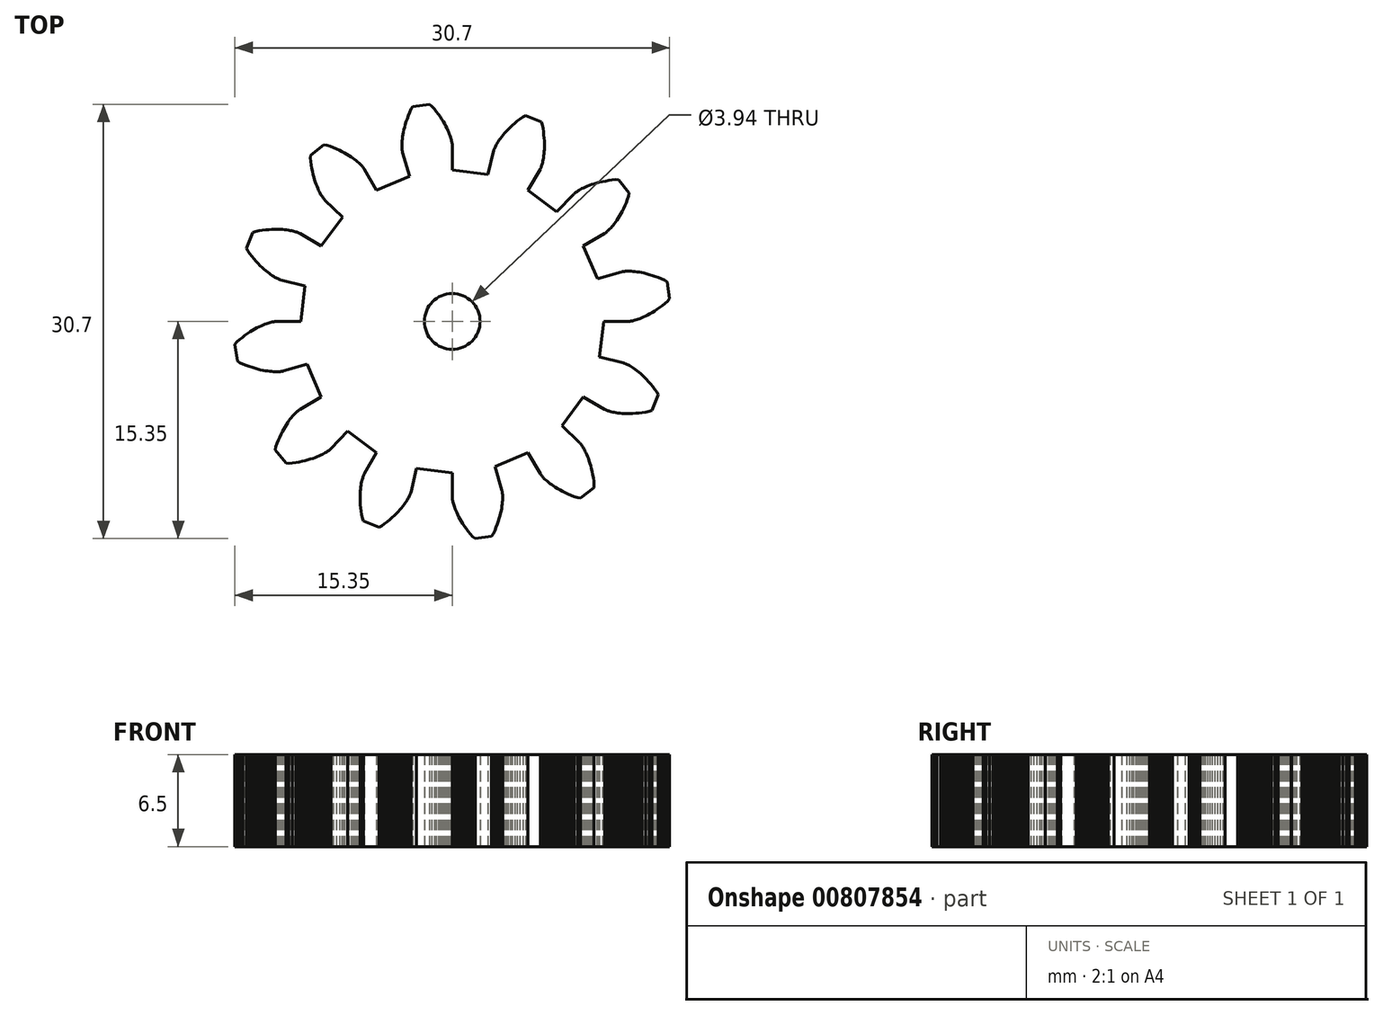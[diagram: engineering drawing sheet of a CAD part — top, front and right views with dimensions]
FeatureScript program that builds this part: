
annotation { "Feature Type Name" : "Feature", "Feature Type Description" : "" }
export const myFeature = defineFeature(function(context is Context, id is Id, definition is map)
    precondition{}
    {
        {
            var Q0;
            Q0=qCreatedBy(makeId("Top.planeOp"),FACE);
            var sketch = newSketch(context, id + "F0", { "sketchPlane" : qUnion([Q0])});
            skLineSegment(sketch, "E0", {"start": v(10.7, 0) * mm, "end": v(12.45, 0) * mm});
            skLineSegment(sketch, "E1", {"start": v(12.45, 0) * mm, "end": v(12.47, 0) * mm});
            skLineSegment(sketch, "E2", {"start": v(12.47, 0) * mm, "end": v(12.5, 0) * mm});
            skLineSegment(sketch, "E3", {"start": v(12.5, 0) * mm, "end": v(12.54, 0) * mm});
            skLineSegment(sketch, "E4", {"start": v(12.54, 0) * mm, "end": v(12.6, 0.02) * mm});
            skLineSegment(sketch, "E5", {"start": v(12.6, 0.02) * mm, "end": v(12.66, 0.03) * mm});
            skLineSegment(sketch, "E6", {"start": v(12.66, 0.03) * mm, "end": v(12.73, 0.04) * mm});
            skLineSegment(sketch, "E7", {"start": v(12.73, 0.04) * mm, "end": v(12.81, 0.06) * mm});
            skLineSegment(sketch, "E8", {"start": v(12.81, 0.06) * mm, "end": v(12.9, 0.09) * mm});
            skLineSegment(sketch, "E9", {"start": v(12.9, 0.09) * mm, "end": v(13, 0.12) * mm});
            skLineSegment(sketch, "E10", {"start": v(13, 0.12) * mm, "end": v(13.12, 0.16) * mm});
            skLineSegment(sketch, "E11", {"start": v(13.12, 0.16) * mm, "end": v(13.24, 0.2) * mm});
            skLineSegment(sketch, "E12", {"start": v(13.24, 0.2) * mm, "end": v(13.37, 0.25) * mm});
            skLineSegment(sketch, "E13", {"start": v(13.37, 0.25) * mm, "end": v(13.5, 0.31) * mm});
            skLineSegment(sketch, "E14", {"start": v(13.5, 0.31) * mm, "end": v(13.65, 0.38) * mm});
            skLineSegment(sketch, "E15", {"start": v(13.65, 0.38) * mm, "end": v(13.8, 0.46) * mm});
            skLineSegment(sketch, "E16", {"start": v(13.8, 0.46) * mm, "end": v(13.96, 0.54) * mm});
            skLineSegment(sketch, "E17", {"start": v(13.96, 0.54) * mm, "end": v(14.12, 0.64) * mm});
            skLineSegment(sketch, "E18", {"start": v(14.12, 0.64) * mm, "end": v(14.3, 0.74) * mm});
            skLineSegment(sketch, "E19", {"start": v(14.3, 0.74) * mm, "end": v(14.47, 0.86) * mm});
            skLineSegment(sketch, "E20", {"start": v(14.47, 0.86) * mm, "end": v(14.65, 0.99) * mm});
            skLineSegment(sketch, "E21", {"start": v(14.65, 0.99) * mm, "end": v(14.83, 1.13) * mm});
            skLineSegment(sketch, "E22", {"start": v(14.83, 1.13) * mm, "end": v(15.02, 1.28) * mm});
            skLineSegment(sketch, "E23", {"start": v(15.02, 1.28) * mm, "end": v(15.22, 1.44) * mm});
            skLineSegment(sketch, "E24", {"start": v(15.22, 1.44) * mm, "end": v(15.35, 1.61) * mm});
            skLineSegment(sketch, "E25", {"start": v(15.35, 1.61) * mm, "end": v(15.18, 2.78) * mm});
            skLineSegment(sketch, "E26", {"start": v(15.18, 2.78) * mm, "end": v(15, 2.9) * mm});
            skLineSegment(sketch, "E27", {"start": v(15, 2.9) * mm, "end": v(14.78, 3) * mm});
            skLineSegment(sketch, "E28", {"start": v(14.78, 3) * mm, "end": v(14.55, 3.1) * mm});
            skLineSegment(sketch, "E29", {"start": v(14.55, 3.1) * mm, "end": v(14.33, 3.18) * mm});
            skLineSegment(sketch, "E30", {"start": v(14.33, 3.18) * mm, "end": v(14.12, 3.25) * mm});
            skLineSegment(sketch, "E31", {"start": v(14.12, 3.25) * mm, "end": v(13.92, 3.32) * mm});
            skLineSegment(sketch, "E32", {"start": v(13.92, 3.32) * mm, "end": v(13.73, 3.37) * mm});
            skLineSegment(sketch, "E33", {"start": v(13.73, 3.37) * mm, "end": v(13.54, 3.41) * mm});
            skLineSegment(sketch, "E34", {"start": v(13.54, 3.41) * mm, "end": v(13.37, 3.45) * mm});
            skLineSegment(sketch, "E35", {"start": v(13.37, 3.45) * mm, "end": v(13.2, 3.48) * mm});
            skLineSegment(sketch, "E36", {"start": v(13.2, 3.48) * mm, "end": v(13.04, 3.5) * mm});
            skLineSegment(sketch, "E37", {"start": v(13.04, 3.5) * mm, "end": v(12.9, 3.53) * mm});
            skLineSegment(sketch, "E38", {"start": v(12.9, 3.53) * mm, "end": v(12.76, 3.54) * mm});
            skLineSegment(sketch, "E39", {"start": v(12.76, 3.54) * mm, "end": v(12.63, 3.55) * mm});
            skLineSegment(sketch, "E40", {"start": v(12.63, 3.55) * mm, "end": v(12.51, 3.55) * mm});
            skLineSegment(sketch, "E41", {"start": v(12.51, 3.55) * mm, "end": v(12.4, 3.55) * mm});
            skLineSegment(sketch, "E42", {"start": v(12.4, 3.55) * mm, "end": v(12.31, 3.55) * mm});
            skLineSegment(sketch, "E43", {"start": v(12.31, 3.55) * mm, "end": v(12.23, 3.55) * mm});
            skLineSegment(sketch, "E44", {"start": v(12.23, 3.55) * mm, "end": v(12.15, 3.54) * mm});
            skLineSegment(sketch, "E45", {"start": v(12.15, 3.54) * mm, "end": v(12.09, 3.53) * mm});
            skLineSegment(sketch, "E46", {"start": v(12.09, 3.53) * mm, "end": v(12.04, 3.53) * mm});
            skLineSegment(sketch, "E47", {"start": v(12.04, 3.53) * mm, "end": v(12, 3.52) * mm});
            skLineSegment(sketch, "E48", {"start": v(12, 3.52) * mm, "end": v(11.96, 3.51) * mm});
            skLineSegment(sketch, "E49", {"start": v(11.96, 3.51) * mm, "end": v(11.94, 3.5) * mm});
            skLineSegment(sketch, "E50", {"start": v(11.94, 3.5) * mm, "end": v(11.93, 3.5) * mm});
            skLineSegment(sketch, "E51", {"start": v(11.93, 3.5) * mm, "end": v(10.26, 3.02) * mm});
            skLineSegment(sketch, "E52", {"start": v(10.26, 3.02) * mm, "end": v(9.26, 5.35) * mm});
            skLineSegment(sketch, "E53", {"start": v(9.26, 5.35) * mm, "end": v(10.77, 6.22) * mm});
            skLineSegment(sketch, "E54", {"start": v(10.77, 6.22) * mm, "end": v(10.78, 6.22) * mm});
            skLineSegment(sketch, "E55", {"start": v(10.78, 6.22) * mm, "end": v(10.8, 6.24) * mm});
            skLineSegment(sketch, "E56", {"start": v(10.8, 6.24) * mm, "end": v(10.82, 6.25) * mm});
            skLineSegment(sketch, "E57", {"start": v(10.82, 6.25) * mm, "end": v(10.86, 6.28) * mm});
            skLineSegment(sketch, "E58", {"start": v(10.86, 6.28) * mm, "end": v(10.9, 6.31) * mm});
            skLineSegment(sketch, "E59", {"start": v(10.9, 6.31) * mm, "end": v(10.95, 6.35) * mm});
            skLineSegment(sketch, "E60", {"start": v(10.95, 6.35) * mm, "end": v(11, 6.4) * mm});
            skLineSegment(sketch, "E61", {"start": v(11, 6.4) * mm, "end": v(11.07, 6.46) * mm});
            skLineSegment(sketch, "E62", {"start": v(11.07, 6.46) * mm, "end": v(11.13, 6.53) * mm});
            skLineSegment(sketch, "E63", {"start": v(11.13, 6.53) * mm, "end": v(11.2, 6.6) * mm});
            skLineSegment(sketch, "E64", {"start": v(11.2, 6.6) * mm, "end": v(11.28, 6.7) * mm});
            skLineSegment(sketch, "E65", {"start": v(11.28, 6.7) * mm, "end": v(11.36, 6.8) * mm});
            skLineSegment(sketch, "E66", {"start": v(11.36, 6.8) * mm, "end": v(11.45, 6.9) * mm});
            skLineSegment(sketch, "E67", {"start": v(11.45, 6.9) * mm, "end": v(11.54, 7.02) * mm});
            skLineSegment(sketch, "E68", {"start": v(11.54, 7.02) * mm, "end": v(11.63, 7.15) * mm});
            skLineSegment(sketch, "E69", {"start": v(11.63, 7.15) * mm, "end": v(11.72, 7.3) * mm});
            skLineSegment(sketch, "E70", {"start": v(11.72, 7.3) * mm, "end": v(11.82, 7.45) * mm});
            skLineSegment(sketch, "E71", {"start": v(11.82, 7.45) * mm, "end": v(11.9, 7.61) * mm});
            skLineSegment(sketch, "E72", {"start": v(11.9, 7.61) * mm, "end": v(12, 7.79) * mm});
            skLineSegment(sketch, "E73", {"start": v(12, 7.79) * mm, "end": v(12.1, 7.98) * mm});
            skLineSegment(sketch, "E74", {"start": v(12.1, 7.98) * mm, "end": v(12.2, 8.18) * mm});
            skLineSegment(sketch, "E75", {"start": v(12.2, 8.18) * mm, "end": v(12.28, 8.4) * mm});
            skLineSegment(sketch, "E76", {"start": v(12.28, 8.4) * mm, "end": v(12.37, 8.62) * mm});
            skLineSegment(sketch, "E77", {"start": v(12.37, 8.62) * mm, "end": v(12.46, 8.86) * mm});
            skLineSegment(sketch, "E78", {"start": v(12.46, 8.86) * mm, "end": v(12.49, 9.07) * mm});
            skLineSegment(sketch, "E79", {"start": v(12.49, 9.07) * mm, "end": v(11.76, 10) * mm});
            skLineSegment(sketch, "E80", {"start": v(11.76, 10) * mm, "end": v(11.54, 10.02) * mm});
            skLineSegment(sketch, "E81", {"start": v(11.54, 10.02) * mm, "end": v(11.3, 10) * mm});
            skLineSegment(sketch, "E82", {"start": v(11.3, 10) * mm, "end": v(11.05, 9.96) * mm});
            skLineSegment(sketch, "E83", {"start": v(11.05, 9.96) * mm, "end": v(10.82, 9.92) * mm});
            skLineSegment(sketch, "E84", {"start": v(10.82, 9.92) * mm, "end": v(10.6, 9.88) * mm});
            skLineSegment(sketch, "E85", {"start": v(10.6, 9.88) * mm, "end": v(10.4, 9.83) * mm});
            skLineSegment(sketch, "E86", {"start": v(10.4, 9.83) * mm, "end": v(10.2, 9.78) * mm});
            skLineSegment(sketch, "E87", {"start": v(10.2, 9.78) * mm, "end": v(10.02, 9.73) * mm});
            skLineSegment(sketch, "E88", {"start": v(10.02, 9.73) * mm, "end": v(9.85, 9.67) * mm});
            skLineSegment(sketch, "E89", {"start": v(9.85, 9.67) * mm, "end": v(9.69, 9.62) * mm});
            skLineSegment(sketch, "E90", {"start": v(9.69, 9.62) * mm, "end": v(9.54, 9.56) * mm});
            skLineSegment(sketch, "E91", {"start": v(9.54, 9.56) * mm, "end": v(9.4, 9.5) * mm});
            skLineSegment(sketch, "E92", {"start": v(9.4, 9.5) * mm, "end": v(9.28, 9.44) * mm});
            skLineSegment(sketch, "E93", {"start": v(9.28, 9.44) * mm, "end": v(9.17, 9.39) * mm});
            skLineSegment(sketch, "E94", {"start": v(9.17, 9.39) * mm, "end": v(9.06, 9.33) * mm});
            skLineSegment(sketch, "E95", {"start": v(9.06, 9.33) * mm, "end": v(8.97, 9.28) * mm});
            skLineSegment(sketch, "E96", {"start": v(8.97, 9.28) * mm, "end": v(8.89, 9.23) * mm});
            skLineSegment(sketch, "E97", {"start": v(8.89, 9.23) * mm, "end": v(8.82, 9.18) * mm});
            skLineSegment(sketch, "E98", {"start": v(8.82, 9.18) * mm, "end": v(8.75, 9.14) * mm});
            skLineSegment(sketch, "E99", {"start": v(8.75, 9.14) * mm, "end": v(8.7, 9.1) * mm});
            skLineSegment(sketch, "E100", {"start": v(8.7, 9.1) * mm, "end": v(8.66, 9.07) * mm});
            skLineSegment(sketch, "E101", {"start": v(8.66, 9.07) * mm, "end": v(8.6, 9.02) * mm});
            skLineSegment(sketch, "E102", {"start": v(8.6, 9.02) * mm, "end": v(8.59, 9) * mm});
            skLineSegment(sketch, "E103", {"start": v(8.59, 9) * mm, "end": v(8.58, 9) * mm});
            skLineSegment(sketch, "E104", {"start": v(8.58, 9) * mm, "end": v(7.38, 7.74) * mm});
            skLineSegment(sketch, "E105", {"start": v(7.38, 7.74) * mm, "end": v(5.35, 9.26) * mm});
            skLineSegment(sketch, "E106", {"start": v(5.35, 9.26) * mm, "end": v(6.22, 10.77) * mm});
            skLineSegment(sketch, "E107", {"start": v(6.22, 10.77) * mm, "end": v(6.22, 10.78) * mm});
            skLineSegment(sketch, "E108", {"start": v(6.22, 10.78) * mm, "end": v(6.23, 10.8) * mm});
            skLineSegment(sketch, "E109", {"start": v(6.23, 10.8) * mm, "end": v(6.25, 10.83) * mm});
            skLineSegment(sketch, "E110", {"start": v(6.25, 10.83) * mm, "end": v(6.26, 10.87) * mm});
            skLineSegment(sketch, "E111", {"start": v(6.26, 10.87) * mm, "end": v(6.28, 10.92) * mm});
            skLineSegment(sketch, "E112", {"start": v(6.28, 10.92) * mm, "end": v(6.3, 10.98) * mm});
            skLineSegment(sketch, "E113", {"start": v(6.3, 10.98) * mm, "end": v(6.33, 11.05) * mm});
            skLineSegment(sketch, "E114", {"start": v(6.33, 11.05) * mm, "end": v(6.35, 11.13) * mm});
            skLineSegment(sketch, "E115", {"start": v(6.35, 11.13) * mm, "end": v(6.38, 11.22) * mm});
            skLineSegment(sketch, "E116", {"start": v(6.38, 11.22) * mm, "end": v(6.4, 11.33) * mm});
            skLineSegment(sketch, "E117", {"start": v(6.4, 11.33) * mm, "end": v(6.42, 11.44) * mm});
            skLineSegment(sketch, "E118", {"start": v(6.42, 11.44) * mm, "end": v(6.45, 11.57) * mm});
            skLineSegment(sketch, "E119", {"start": v(6.45, 11.57) * mm, "end": v(6.46, 11.7) * mm});
            skLineSegment(sketch, "E120", {"start": v(6.46, 11.7) * mm, "end": v(6.48, 11.85) * mm});
            skLineSegment(sketch, "E121", {"start": v(6.48, 11.85) * mm, "end": v(6.5, 12) * mm});
            skLineSegment(sketch, "E122", {"start": v(6.5, 12) * mm, "end": v(6.5, 12.18) * mm});
            skLineSegment(sketch, "E123", {"start": v(6.5, 12.18) * mm, "end": v(6.5, 12.36) * mm});
            skLineSegment(sketch, "E124", {"start": v(6.5, 12.36) * mm, "end": v(6.5, 12.55) * mm});
            skLineSegment(sketch, "E125", {"start": v(6.5, 12.55) * mm, "end": v(6.5, 12.75) * mm});
            skLineSegment(sketch, "E126", {"start": v(6.5, 12.75) * mm, "end": v(6.49, 12.96) * mm});
            skLineSegment(sketch, "E127", {"start": v(6.49, 12.96) * mm, "end": v(6.47, 13.18) * mm});
            skLineSegment(sketch, "E128", {"start": v(6.47, 13.18) * mm, "end": v(6.44, 13.41) * mm});
            skLineSegment(sketch, "E129", {"start": v(6.44, 13.41) * mm, "end": v(6.4, 13.65) * mm});
            skLineSegment(sketch, "E130", {"start": v(6.4, 13.65) * mm, "end": v(6.36, 13.9) * mm});
            skLineSegment(sketch, "E131", {"start": v(6.36, 13.9) * mm, "end": v(6.28, 14.1) * mm});
            skLineSegment(sketch, "E132", {"start": v(6.28, 14.1) * mm, "end": v(5.18, 14.54) * mm});
            skLineSegment(sketch, "E133", {"start": v(5.18, 14.54) * mm, "end": v(4.99, 14.45) * mm});
            skLineSegment(sketch, "E134", {"start": v(4.99, 14.45) * mm, "end": v(4.78, 14.3) * mm});
            skLineSegment(sketch, "E135", {"start": v(4.78, 14.3) * mm, "end": v(4.6, 14.15) * mm});
            skLineSegment(sketch, "E136", {"start": v(4.6, 14.15) * mm, "end": v(4.41, 14) * mm});
            skLineSegment(sketch, "E137", {"start": v(4.41, 14) * mm, "end": v(4.24, 13.86) * mm});
            skLineSegment(sketch, "E138", {"start": v(4.24, 13.86) * mm, "end": v(4.09, 13.71) * mm});
            skLineSegment(sketch, "E139", {"start": v(4.09, 13.71) * mm, "end": v(3.95, 13.57) * mm});
            skLineSegment(sketch, "E140", {"start": v(3.95, 13.57) * mm, "end": v(3.81, 13.43) * mm});
            skLineSegment(sketch, "E141", {"start": v(3.81, 13.43) * mm, "end": v(3.7, 13.3) * mm});
            skLineSegment(sketch, "E142", {"start": v(3.7, 13.3) * mm, "end": v(3.58, 13.17) * mm});
            skLineSegment(sketch, "E143", {"start": v(3.58, 13.17) * mm, "end": v(3.48, 13.05) * mm});
            skLineSegment(sketch, "E144", {"start": v(3.48, 13.05) * mm, "end": v(3.4, 12.93) * mm});
            skLineSegment(sketch, "E145", {"start": v(3.4, 12.93) * mm, "end": v(3.31, 12.82) * mm});
            skLineSegment(sketch, "E146", {"start": v(3.31, 12.82) * mm, "end": v(3.24, 12.71) * mm});
            skLineSegment(sketch, "E147", {"start": v(3.24, 12.71) * mm, "end": v(3.18, 12.61) * mm});
            skLineSegment(sketch, "E148", {"start": v(3.18, 12.61) * mm, "end": v(3.13, 12.52) * mm});
            skLineSegment(sketch, "E149", {"start": v(3.13, 12.52) * mm, "end": v(3.08, 12.44) * mm});
            skLineSegment(sketch, "E150", {"start": v(3.08, 12.44) * mm, "end": v(3.04, 12.36) * mm});
            skLineSegment(sketch, "E151", {"start": v(3.04, 12.36) * mm, "end": v(3, 12.3) * mm});
            skLineSegment(sketch, "E152", {"start": v(3, 12.3) * mm, "end": v(2.98, 12.24) * mm});
            skLineSegment(sketch, "E153", {"start": v(2.98, 12.24) * mm, "end": v(2.96, 12.19) * mm});
            skLineSegment(sketch, "E154", {"start": v(2.96, 12.19) * mm, "end": v(2.95, 12.15) * mm});
            skLineSegment(sketch, "E155", {"start": v(2.95, 12.15) * mm, "end": v(2.94, 12.12) * mm});
            skLineSegment(sketch, "E156", {"start": v(2.94, 12.12) * mm, "end": v(2.93, 12.1) * mm});
            skLineSegment(sketch, "E157", {"start": v(2.93, 12.1) * mm, "end": v(2.93, 12.08) * mm});
            skLineSegment(sketch, "E158", {"start": v(2.93, 12.08) * mm, "end": v(2.52, 10.4) * mm});
            skLineSegment(sketch, "E159", {"start": v(2.52, 10.4) * mm, "end": v(0, 10.7) * mm});
            skLineSegment(sketch, "E160", {"start": v(0, 10.7) * mm, "end": v(0, 12.45) * mm});
            skLineSegment(sketch, "E161", {"start": v(0, 12.45) * mm, "end": v(0, 12.47) * mm});
            skLineSegment(sketch, "E162", {"start": v(0, 12.47) * mm, "end": v(0, 12.5) * mm});
            skLineSegment(sketch, "E163", {"start": v(0, 12.5) * mm, "end": v(0, 12.54) * mm});
            skLineSegment(sketch, "E164", {"start": v(0, 12.54) * mm, "end": v(-0.02, 12.6) * mm});
            skLineSegment(sketch, "E165", {"start": v(-0.02, 12.6) * mm, "end": v(-0.03, 12.66) * mm});
            skLineSegment(sketch, "E166", {"start": v(-0.03, 12.66) * mm, "end": v(-0.04, 12.73) * mm});
            skLineSegment(sketch, "E167", {"start": v(-0.04, 12.73) * mm, "end": v(-0.06, 12.81) * mm});
            skLineSegment(sketch, "E168", {"start": v(-0.06, 12.81) * mm, "end": v(-0.09, 12.9) * mm});
            skLineSegment(sketch, "E169", {"start": v(-0.09, 12.9) * mm, "end": v(-0.12, 13) * mm});
            skLineSegment(sketch, "E170", {"start": v(-0.12, 13) * mm, "end": v(-0.16, 13.12) * mm});
            skLineSegment(sketch, "E171", {"start": v(-0.16, 13.12) * mm, "end": v(-0.2, 13.24) * mm});
            skLineSegment(sketch, "E172", {"start": v(-0.2, 13.24) * mm, "end": v(-0.25, 13.37) * mm});
            skLineSegment(sketch, "E173", {"start": v(-0.25, 13.37) * mm, "end": v(-0.31, 13.5) * mm});
            skLineSegment(sketch, "E174", {"start": v(-0.31, 13.5) * mm, "end": v(-0.38, 13.65) * mm});
            skLineSegment(sketch, "E175", {"start": v(-0.38, 13.65) * mm, "end": v(-0.46, 13.8) * mm});
            skLineSegment(sketch, "E176", {"start": v(-0.46, 13.8) * mm, "end": v(-0.54, 13.96) * mm});
            skLineSegment(sketch, "E177", {"start": v(-0.54, 13.96) * mm, "end": v(-0.64, 14.12) * mm});
            skLineSegment(sketch, "E178", {"start": v(-0.64, 14.12) * mm, "end": v(-0.74, 14.3) * mm});
            skLineSegment(sketch, "E179", {"start": v(-0.74, 14.3) * mm, "end": v(-0.86, 14.47) * mm});
            skLineSegment(sketch, "E180", {"start": v(-0.86, 14.47) * mm, "end": v(-0.99, 14.65) * mm});
            skLineSegment(sketch, "E181", {"start": v(-0.99, 14.65) * mm, "end": v(-1.13, 14.83) * mm});
            skLineSegment(sketch, "E182", {"start": v(-1.13, 14.83) * mm, "end": v(-1.28, 15.02) * mm});
            skLineSegment(sketch, "E183", {"start": v(-1.28, 15.02) * mm, "end": v(-1.44, 15.22) * mm});
            skLineSegment(sketch, "E184", {"start": v(-1.44, 15.22) * mm, "end": v(-1.61, 15.35) * mm});
            skLineSegment(sketch, "E185", {"start": v(-1.61, 15.35) * mm, "end": v(-2.78, 15.18) * mm});
            skLineSegment(sketch, "E186", {"start": v(-2.78, 15.18) * mm, "end": v(-2.9, 15) * mm});
            skLineSegment(sketch, "E187", {"start": v(-2.9, 15) * mm, "end": v(-3, 14.78) * mm});
            skLineSegment(sketch, "E188", {"start": v(-3, 14.78) * mm, "end": v(-3.1, 14.55) * mm});
            skLineSegment(sketch, "E189", {"start": v(-3.1, 14.55) * mm, "end": v(-3.18, 14.33) * mm});
            skLineSegment(sketch, "E190", {"start": v(-3.18, 14.33) * mm, "end": v(-3.25, 14.12) * mm});
            skLineSegment(sketch, "E191", {"start": v(-3.25, 14.12) * mm, "end": v(-3.32, 13.92) * mm});
            skLineSegment(sketch, "E192", {"start": v(-3.32, 13.92) * mm, "end": v(-3.37, 13.73) * mm});
            skLineSegment(sketch, "E193", {"start": v(-3.37, 13.73) * mm, "end": v(-3.41, 13.54) * mm});
            skLineSegment(sketch, "E194", {"start": v(-3.41, 13.54) * mm, "end": v(-3.45, 13.37) * mm});
            skLineSegment(sketch, "E195", {"start": v(-3.45, 13.37) * mm, "end": v(-3.48, 13.2) * mm});
            skLineSegment(sketch, "E196", {"start": v(-3.48, 13.2) * mm, "end": v(-3.5, 13.04) * mm});
            skLineSegment(sketch, "E197", {"start": v(-3.5, 13.04) * mm, "end": v(-3.53, 12.9) * mm});
            skLineSegment(sketch, "E198", {"start": v(-3.53, 12.9) * mm, "end": v(-3.54, 12.76) * mm});
            skLineSegment(sketch, "E199", {"start": v(-3.54, 12.76) * mm, "end": v(-3.55, 12.63) * mm});
            skLineSegment(sketch, "E200", {"start": v(-3.55, 12.63) * mm, "end": v(-3.55, 12.51) * mm});
            skLineSegment(sketch, "E201", {"start": v(-3.55, 12.51) * mm, "end": v(-3.55, 12.4) * mm});
            skLineSegment(sketch, "E202", {"start": v(-3.55, 12.4) * mm, "end": v(-3.55, 12.31) * mm});
            skLineSegment(sketch, "E203", {"start": v(-3.55, 12.31) * mm, "end": v(-3.55, 12.23) * mm});
            skLineSegment(sketch, "E204", {"start": v(-3.55, 12.23) * mm, "end": v(-3.54, 12.15) * mm});
            skLineSegment(sketch, "E205", {"start": v(-3.54, 12.15) * mm, "end": v(-3.53, 12.09) * mm});
            skLineSegment(sketch, "E206", {"start": v(-3.53, 12.09) * mm, "end": v(-3.53, 12.04) * mm});
            skLineSegment(sketch, "E207", {"start": v(-3.53, 12.04) * mm, "end": v(-3.52, 12) * mm});
            skLineSegment(sketch, "E208", {"start": v(-3.52, 12) * mm, "end": v(-3.51, 11.96) * mm});
            skLineSegment(sketch, "E209", {"start": v(-3.51, 11.96) * mm, "end": v(-3.5, 11.94) * mm});
            skLineSegment(sketch, "E210", {"start": v(-3.5, 11.94) * mm, "end": v(-3.5, 11.93) * mm});
            skLineSegment(sketch, "E211", {"start": v(-3.5, 11.93) * mm, "end": v(-3.02, 10.26) * mm});
            skLineSegment(sketch, "E212", {"start": v(-3.02, 10.26) * mm, "end": v(-5.35, 9.26) * mm});
            skLineSegment(sketch, "E213", {"start": v(-5.35, 9.26) * mm, "end": v(-6.22, 10.77) * mm});
            skLineSegment(sketch, "E214", {"start": v(-6.22, 10.77) * mm, "end": v(-6.22, 10.78) * mm});
            skLineSegment(sketch, "E215", {"start": v(-6.22, 10.78) * mm, "end": v(-6.24, 10.8) * mm});
            skLineSegment(sketch, "E216", {"start": v(-6.24, 10.8) * mm, "end": v(-6.25, 10.82) * mm});
            skLineSegment(sketch, "E217", {"start": v(-6.25, 10.82) * mm, "end": v(-6.28, 10.86) * mm});
            skLineSegment(sketch, "E218", {"start": v(-6.28, 10.86) * mm, "end": v(-6.31, 10.9) * mm});
            skLineSegment(sketch, "E219", {"start": v(-6.31, 10.9) * mm, "end": v(-6.35, 10.95) * mm});
            skLineSegment(sketch, "E220", {"start": v(-6.35, 10.95) * mm, "end": v(-6.4, 11) * mm});
            skLineSegment(sketch, "E221", {"start": v(-6.4, 11) * mm, "end": v(-6.46, 11.07) * mm});
            skLineSegment(sketch, "E222", {"start": v(-6.46, 11.07) * mm, "end": v(-6.53, 11.13) * mm});
            skLineSegment(sketch, "E223", {"start": v(-6.53, 11.13) * mm, "end": v(-6.6, 11.2) * mm});
            skLineSegment(sketch, "E224", {"start": v(-6.6, 11.2) * mm, "end": v(-6.7, 11.28) * mm});
            skLineSegment(sketch, "E225", {"start": v(-6.7, 11.28) * mm, "end": v(-6.8, 11.36) * mm});
            skLineSegment(sketch, "E226", {"start": v(-6.8, 11.36) * mm, "end": v(-6.9, 11.45) * mm});
            skLineSegment(sketch, "E227", {"start": v(-6.9, 11.45) * mm, "end": v(-7.02, 11.54) * mm});
            skLineSegment(sketch, "E228", {"start": v(-7.02, 11.54) * mm, "end": v(-7.15, 11.63) * mm});
            skLineSegment(sketch, "E229", {"start": v(-7.15, 11.63) * mm, "end": v(-7.3, 11.72) * mm});
            skLineSegment(sketch, "E230", {"start": v(-7.3, 11.72) * mm, "end": v(-7.45, 11.82) * mm});
            skLineSegment(sketch, "E231", {"start": v(-7.45, 11.82) * mm, "end": v(-7.61, 11.9) * mm});
            skLineSegment(sketch, "E232", {"start": v(-7.61, 11.9) * mm, "end": v(-7.79, 12) * mm});
            skLineSegment(sketch, "E233", {"start": v(-7.79, 12) * mm, "end": v(-7.98, 12.1) * mm});
            skLineSegment(sketch, "E234", {"start": v(-7.98, 12.1) * mm, "end": v(-8.18, 12.2) * mm});
            skLineSegment(sketch, "E235", {"start": v(-8.18, 12.2) * mm, "end": v(-8.4, 12.28) * mm});
            skLineSegment(sketch, "E236", {"start": v(-8.4, 12.28) * mm, "end": v(-8.62, 12.37) * mm});
            skLineSegment(sketch, "E237", {"start": v(-8.62, 12.37) * mm, "end": v(-8.86, 12.46) * mm});
            skLineSegment(sketch, "E238", {"start": v(-8.86, 12.46) * mm, "end": v(-9.07, 12.49) * mm});
            skLineSegment(sketch, "E239", {"start": v(-9.07, 12.49) * mm, "end": v(-10, 11.76) * mm});
            skLineSegment(sketch, "E240", {"start": v(-10, 11.76) * mm, "end": v(-10.02, 11.54) * mm});
            skLineSegment(sketch, "E241", {"start": v(-10.02, 11.54) * mm, "end": v(-10, 11.3) * mm});
            skLineSegment(sketch, "E242", {"start": v(-10, 11.3) * mm, "end": v(-9.96, 11.05) * mm});
            skLineSegment(sketch, "E243", {"start": v(-9.96, 11.05) * mm, "end": v(-9.92, 10.82) * mm});
            skLineSegment(sketch, "E244", {"start": v(-9.92, 10.82) * mm, "end": v(-9.88, 10.6) * mm});
            skLineSegment(sketch, "E245", {"start": v(-9.88, 10.6) * mm, "end": v(-9.83, 10.4) * mm});
            skLineSegment(sketch, "E246", {"start": v(-9.83, 10.4) * mm, "end": v(-9.78, 10.2) * mm});
            skLineSegment(sketch, "E247", {"start": v(-9.78, 10.2) * mm, "end": v(-9.73, 10.02) * mm});
            skLineSegment(sketch, "E248", {"start": v(-9.73, 10.02) * mm, "end": v(-9.67, 9.85) * mm});
            skLineSegment(sketch, "E249", {"start": v(-9.67, 9.85) * mm, "end": v(-9.62, 9.69) * mm});
            skLineSegment(sketch, "E250", {"start": v(-9.62, 9.69) * mm, "end": v(-9.56, 9.54) * mm});
            skLineSegment(sketch, "E251", {"start": v(-9.56, 9.54) * mm, "end": v(-9.5, 9.4) * mm});
            skLineSegment(sketch, "E252", {"start": v(-9.5, 9.4) * mm, "end": v(-9.44, 9.28) * mm});
            skLineSegment(sketch, "E253", {"start": v(-9.44, 9.28) * mm, "end": v(-9.39, 9.17) * mm});
            skLineSegment(sketch, "E254", {"start": v(-9.39, 9.17) * mm, "end": v(-9.33, 9.06) * mm});
            skLineSegment(sketch, "E255", {"start": v(-9.33, 9.06) * mm, "end": v(-9.28, 8.97) * mm});
            skLineSegment(sketch, "E256", {"start": v(-9.28, 8.97) * mm, "end": v(-9.23, 8.89) * mm});
            skLineSegment(sketch, "E257", {"start": v(-9.23, 8.89) * mm, "end": v(-9.18, 8.82) * mm});
            skLineSegment(sketch, "E258", {"start": v(-9.18, 8.82) * mm, "end": v(-9.14, 8.75) * mm});
            skLineSegment(sketch, "E259", {"start": v(-9.14, 8.75) * mm, "end": v(-9.1, 8.7) * mm});
            skLineSegment(sketch, "E260", {"start": v(-9.1, 8.7) * mm, "end": v(-9.07, 8.66) * mm});
            skLineSegment(sketch, "E261", {"start": v(-9.07, 8.66) * mm, "end": v(-9.02, 8.6) * mm});
            skLineSegment(sketch, "E262", {"start": v(-9.02, 8.6) * mm, "end": v(-9, 8.59) * mm});
            skLineSegment(sketch, "E263", {"start": v(-9, 8.59) * mm, "end": v(-9, 8.58) * mm});
            skLineSegment(sketch, "E264", {"start": v(-9, 8.58) * mm, "end": v(-7.74, 7.38) * mm});
            skLineSegment(sketch, "E265", {"start": v(-7.74, 7.38) * mm, "end": v(-9.26, 5.35) * mm});
            skLineSegment(sketch, "E266", {"start": v(-9.26, 5.35) * mm, "end": v(-10.77, 6.22) * mm});
            skLineSegment(sketch, "E267", {"start": v(-10.77, 6.22) * mm, "end": v(-10.78, 6.22) * mm});
            skLineSegment(sketch, "E268", {"start": v(-10.78, 6.22) * mm, "end": v(-10.8, 6.23) * mm});
            skLineSegment(sketch, "E269", {"start": v(-10.8, 6.23) * mm, "end": v(-10.83, 6.25) * mm});
            skLineSegment(sketch, "E270", {"start": v(-10.83, 6.25) * mm, "end": v(-10.87, 6.26) * mm});
            skLineSegment(sketch, "E271", {"start": v(-10.87, 6.26) * mm, "end": v(-10.92, 6.28) * mm});
            skLineSegment(sketch, "E272", {"start": v(-10.92, 6.28) * mm, "end": v(-10.98, 6.3) * mm});
            skLineSegment(sketch, "E273", {"start": v(-10.98, 6.3) * mm, "end": v(-11.05, 6.33) * mm});
            skLineSegment(sketch, "E274", {"start": v(-11.05, 6.33) * mm, "end": v(-11.13, 6.35) * mm});
            skLineSegment(sketch, "E275", {"start": v(-11.13, 6.35) * mm, "end": v(-11.22, 6.38) * mm});
            skLineSegment(sketch, "E276", {"start": v(-11.22, 6.38) * mm, "end": v(-11.33, 6.4) * mm});
            skLineSegment(sketch, "E277", {"start": v(-11.33, 6.4) * mm, "end": v(-11.44, 6.42) * mm});
            skLineSegment(sketch, "E278", {"start": v(-11.44, 6.42) * mm, "end": v(-11.57, 6.45) * mm});
            skLineSegment(sketch, "E279", {"start": v(-11.57, 6.45) * mm, "end": v(-11.7, 6.46) * mm});
            skLineSegment(sketch, "E280", {"start": v(-11.7, 6.46) * mm, "end": v(-11.85, 6.48) * mm});
            skLineSegment(sketch, "E281", {"start": v(-11.85, 6.48) * mm, "end": v(-12, 6.5) * mm});
            skLineSegment(sketch, "E282", {"start": v(-12, 6.5) * mm, "end": v(-12.18, 6.5) * mm});
            skLineSegment(sketch, "E283", {"start": v(-12.18, 6.5) * mm, "end": v(-12.36, 6.5) * mm});
            skLineSegment(sketch, "E284", {"start": v(-12.36, 6.5) * mm, "end": v(-12.55, 6.5) * mm});
            skLineSegment(sketch, "E285", {"start": v(-12.55, 6.5) * mm, "end": v(-12.75, 6.5) * mm});
            skLineSegment(sketch, "E286", {"start": v(-12.75, 6.5) * mm, "end": v(-12.96, 6.49) * mm});
            skLineSegment(sketch, "E287", {"start": v(-12.96, 6.49) * mm, "end": v(-13.18, 6.47) * mm});
            skLineSegment(sketch, "E288", {"start": v(-13.18, 6.47) * mm, "end": v(-13.41, 6.44) * mm});
            skLineSegment(sketch, "E289", {"start": v(-13.41, 6.44) * mm, "end": v(-13.65, 6.4) * mm});
            skLineSegment(sketch, "E290", {"start": v(-13.65, 6.4) * mm, "end": v(-13.9, 6.36) * mm});
            skLineSegment(sketch, "E291", {"start": v(-13.9, 6.36) * mm, "end": v(-14.1, 6.28) * mm});
            skLineSegment(sketch, "E292", {"start": v(-14.1, 6.28) * mm, "end": v(-14.54, 5.18) * mm});
            skLineSegment(sketch, "E293", {"start": v(-14.54, 5.18) * mm, "end": v(-14.45, 4.99) * mm});
            skLineSegment(sketch, "E294", {"start": v(-14.45, 4.99) * mm, "end": v(-14.3, 4.78) * mm});
            skLineSegment(sketch, "E295", {"start": v(-14.3, 4.78) * mm, "end": v(-14.15, 4.6) * mm});
            skLineSegment(sketch, "E296", {"start": v(-14.15, 4.6) * mm, "end": v(-14, 4.41) * mm});
            skLineSegment(sketch, "E297", {"start": v(-14, 4.41) * mm, "end": v(-13.86, 4.24) * mm});
            skLineSegment(sketch, "E298", {"start": v(-13.86, 4.24) * mm, "end": v(-13.71, 4.09) * mm});
            skLineSegment(sketch, "E299", {"start": v(-13.71, 4.09) * mm, "end": v(-13.57, 3.95) * mm});
            skLineSegment(sketch, "E300", {"start": v(-13.57, 3.95) * mm, "end": v(-13.43, 3.81) * mm});
            skLineSegment(sketch, "E301", {"start": v(-13.43, 3.81) * mm, "end": v(-13.3, 3.7) * mm});
            skLineSegment(sketch, "E302", {"start": v(-13.3, 3.7) * mm, "end": v(-13.17, 3.58) * mm});
            skLineSegment(sketch, "E303", {"start": v(-13.17, 3.58) * mm, "end": v(-13.05, 3.48) * mm});
            skLineSegment(sketch, "E304", {"start": v(-13.05, 3.48) * mm, "end": v(-12.93, 3.4) * mm});
            skLineSegment(sketch, "E305", {"start": v(-12.93, 3.4) * mm, "end": v(-12.82, 3.31) * mm});
            skLineSegment(sketch, "E306", {"start": v(-12.82, 3.31) * mm, "end": v(-12.71, 3.24) * mm});
            skLineSegment(sketch, "E307", {"start": v(-12.71, 3.24) * mm, "end": v(-12.61, 3.18) * mm});
            skLineSegment(sketch, "E308", {"start": v(-12.61, 3.18) * mm, "end": v(-12.52, 3.13) * mm});
            skLineSegment(sketch, "E309", {"start": v(-12.52, 3.13) * mm, "end": v(-12.44, 3.08) * mm});
            skLineSegment(sketch, "E310", {"start": v(-12.44, 3.08) * mm, "end": v(-12.36, 3.04) * mm});
            skLineSegment(sketch, "E311", {"start": v(-12.36, 3.04) * mm, "end": v(-12.3, 3) * mm});
            skLineSegment(sketch, "E312", {"start": v(-12.3, 3) * mm, "end": v(-12.24, 2.98) * mm});
            skLineSegment(sketch, "E313", {"start": v(-12.24, 2.98) * mm, "end": v(-12.19, 2.96) * mm});
            skLineSegment(sketch, "E314", {"start": v(-12.19, 2.96) * mm, "end": v(-12.15, 2.95) * mm});
            skLineSegment(sketch, "E315", {"start": v(-12.15, 2.95) * mm, "end": v(-12.12, 2.94) * mm});
            skLineSegment(sketch, "E316", {"start": v(-12.12, 2.94) * mm, "end": v(-12.1, 2.93) * mm});
            skLineSegment(sketch, "E317", {"start": v(-12.1, 2.93) * mm, "end": v(-12.08, 2.93) * mm});
            skLineSegment(sketch, "E318", {"start": v(-12.08, 2.93) * mm, "end": v(-10.4, 2.52) * mm});
            skLineSegment(sketch, "E319", {"start": v(-10.4, 2.52) * mm, "end": v(-10.7, 0) * mm});
            skLineSegment(sketch, "E320", {"start": v(-10.7, 0) * mm, "end": v(-12.45, 0) * mm});
            skLineSegment(sketch, "E321", {"start": v(-12.45, 0) * mm, "end": v(-12.47, 0) * mm});
            skLineSegment(sketch, "E322", {"start": v(-12.47, 0) * mm, "end": v(-12.5, 0) * mm});
            skLineSegment(sketch, "E323", {"start": v(-12.5, 0) * mm, "end": v(-12.54, 0) * mm});
            skLineSegment(sketch, "E324", {"start": v(-12.54, 0) * mm, "end": v(-12.6, -0.02) * mm});
            skLineSegment(sketch, "E325", {"start": v(-12.6, -0.02) * mm, "end": v(-12.66, -0.03) * mm});
            skLineSegment(sketch, "E326", {"start": v(-12.66, -0.03) * mm, "end": v(-12.73, -0.04) * mm});
            skLineSegment(sketch, "E327", {"start": v(-12.73, -0.04) * mm, "end": v(-12.81, -0.06) * mm});
            skLineSegment(sketch, "E328", {"start": v(-12.81, -0.06) * mm, "end": v(-12.9, -0.09) * mm});
            skLineSegment(sketch, "E329", {"start": v(-12.9, -0.09) * mm, "end": v(-13, -0.12) * mm});
            skLineSegment(sketch, "E330", {"start": v(-13, -0.12) * mm, "end": v(-13.12, -0.16) * mm});
            skLineSegment(sketch, "E331", {"start": v(-13.12, -0.16) * mm, "end": v(-13.24, -0.2) * mm});
            skLineSegment(sketch, "E332", {"start": v(-13.24, -0.2) * mm, "end": v(-13.37, -0.25) * mm});
            skLineSegment(sketch, "E333", {"start": v(-13.37, -0.25) * mm, "end": v(-13.5, -0.31) * mm});
            skLineSegment(sketch, "E334", {"start": v(-13.5, -0.31) * mm, "end": v(-13.65, -0.38) * mm});
            skLineSegment(sketch, "E335", {"start": v(-13.65, -0.38) * mm, "end": v(-13.8, -0.46) * mm});
            skLineSegment(sketch, "E336", {"start": v(-13.8, -0.46) * mm, "end": v(-13.96, -0.54) * mm});
            skLineSegment(sketch, "E337", {"start": v(-13.96, -0.54) * mm, "end": v(-14.12, -0.64) * mm});
            skLineSegment(sketch, "E338", {"start": v(-14.12, -0.64) * mm, "end": v(-14.3, -0.74) * mm});
            skLineSegment(sketch, "E339", {"start": v(-14.3, -0.74) * mm, "end": v(-14.47, -0.86) * mm});
            skLineSegment(sketch, "E340", {"start": v(-14.47, -0.86) * mm, "end": v(-14.65, -0.99) * mm});
            skLineSegment(sketch, "E341", {"start": v(-14.65, -0.99) * mm, "end": v(-14.83, -1.13) * mm});
            skLineSegment(sketch, "E342", {"start": v(-14.83, -1.13) * mm, "end": v(-15.02, -1.28) * mm});
            skLineSegment(sketch, "E343", {"start": v(-15.02, -1.28) * mm, "end": v(-15.22, -1.44) * mm});
            skLineSegment(sketch, "E344", {"start": v(-15.22, -1.44) * mm, "end": v(-15.35, -1.61) * mm});
            skLineSegment(sketch, "E345", {"start": v(-15.35, -1.61) * mm, "end": v(-15.18, -2.78) * mm});
            skLineSegment(sketch, "E346", {"start": v(-15.18, -2.78) * mm, "end": v(-15, -2.9) * mm});
            skLineSegment(sketch, "E347", {"start": v(-15, -2.9) * mm, "end": v(-14.78, -3) * mm});
            skLineSegment(sketch, "E348", {"start": v(-14.78, -3) * mm, "end": v(-14.55, -3.1) * mm});
            skLineSegment(sketch, "E349", {"start": v(-14.55, -3.1) * mm, "end": v(-14.33, -3.18) * mm});
            skLineSegment(sketch, "E350", {"start": v(-14.33, -3.18) * mm, "end": v(-14.12, -3.25) * mm});
            skLineSegment(sketch, "E351", {"start": v(-14.12, -3.25) * mm, "end": v(-13.92, -3.32) * mm});
            skLineSegment(sketch, "E352", {"start": v(-13.92, -3.32) * mm, "end": v(-13.73, -3.37) * mm});
            skLineSegment(sketch, "E353", {"start": v(-13.73, -3.37) * mm, "end": v(-13.54, -3.41) * mm});
            skLineSegment(sketch, "E354", {"start": v(-13.54, -3.41) * mm, "end": v(-13.37, -3.45) * mm});
            skLineSegment(sketch, "E355", {"start": v(-13.37, -3.45) * mm, "end": v(-13.2, -3.48) * mm});
            skLineSegment(sketch, "E356", {"start": v(-13.2, -3.48) * mm, "end": v(-13.04, -3.5) * mm});
            skLineSegment(sketch, "E357", {"start": v(-13.04, -3.5) * mm, "end": v(-12.9, -3.53) * mm});
            skLineSegment(sketch, "E358", {"start": v(-12.9, -3.53) * mm, "end": v(-12.76, -3.54) * mm});
            skLineSegment(sketch, "E359", {"start": v(-12.76, -3.54) * mm, "end": v(-12.63, -3.55) * mm});
            skLineSegment(sketch, "E360", {"start": v(-12.63, -3.55) * mm, "end": v(-12.51, -3.55) * mm});
            skLineSegment(sketch, "E361", {"start": v(-12.51, -3.55) * mm, "end": v(-12.4, -3.55) * mm});
            skLineSegment(sketch, "E362", {"start": v(-12.4, -3.55) * mm, "end": v(-12.31, -3.55) * mm});
            skLineSegment(sketch, "E363", {"start": v(-12.31, -3.55) * mm, "end": v(-12.23, -3.55) * mm});
            skLineSegment(sketch, "E364", {"start": v(-12.23, -3.55) * mm, "end": v(-12.15, -3.54) * mm});
            skLineSegment(sketch, "E365", {"start": v(-12.15, -3.54) * mm, "end": v(-12.09, -3.53) * mm});
            skLineSegment(sketch, "E366", {"start": v(-12.09, -3.53) * mm, "end": v(-12.04, -3.53) * mm});
            skLineSegment(sketch, "E367", {"start": v(-12.04, -3.53) * mm, "end": v(-12, -3.52) * mm});
            skLineSegment(sketch, "E368", {"start": v(-12, -3.52) * mm, "end": v(-11.96, -3.51) * mm});
            skLineSegment(sketch, "E369", {"start": v(-11.96, -3.51) * mm, "end": v(-11.94, -3.5) * mm});
            skLineSegment(sketch, "E370", {"start": v(-11.94, -3.5) * mm, "end": v(-11.93, -3.5) * mm});
            skLineSegment(sketch, "E371", {"start": v(-11.93, -3.5) * mm, "end": v(-10.26, -3.02) * mm});
            skLineSegment(sketch, "E372", {"start": v(-10.26, -3.02) * mm, "end": v(-9.26, -5.35) * mm});
            skLineSegment(sketch, "E373", {"start": v(-9.26, -5.35) * mm, "end": v(-10.77, -6.22) * mm});
            skLineSegment(sketch, "E374", {"start": v(-10.77, -6.22) * mm, "end": v(-10.78, -6.22) * mm});
            skLineSegment(sketch, "E375", {"start": v(-10.78, -6.22) * mm, "end": v(-10.8, -6.24) * mm});
            skLineSegment(sketch, "E376", {"start": v(-10.8, -6.24) * mm, "end": v(-10.82, -6.25) * mm});
            skLineSegment(sketch, "E377", {"start": v(-10.82, -6.25) * mm, "end": v(-10.86, -6.28) * mm});
            skLineSegment(sketch, "E378", {"start": v(-10.86, -6.28) * mm, "end": v(-10.9, -6.31) * mm});
            skLineSegment(sketch, "E379", {"start": v(-10.9, -6.31) * mm, "end": v(-10.95, -6.35) * mm});
            skLineSegment(sketch, "E380", {"start": v(-10.95, -6.35) * mm, "end": v(-11, -6.4) * mm});
            skLineSegment(sketch, "E381", {"start": v(-11, -6.4) * mm, "end": v(-11.07, -6.46) * mm});
            skLineSegment(sketch, "E382", {"start": v(-11.07, -6.46) * mm, "end": v(-11.13, -6.53) * mm});
            skLineSegment(sketch, "E383", {"start": v(-11.13, -6.53) * mm, "end": v(-11.2, -6.6) * mm});
            skLineSegment(sketch, "E384", {"start": v(-11.2, -6.6) * mm, "end": v(-11.28, -6.7) * mm});
            skLineSegment(sketch, "E385", {"start": v(-11.28, -6.7) * mm, "end": v(-11.36, -6.8) * mm});
            skLineSegment(sketch, "E386", {"start": v(-11.36, -6.8) * mm, "end": v(-11.45, -6.9) * mm});
            skLineSegment(sketch, "E387", {"start": v(-11.45, -6.9) * mm, "end": v(-11.54, -7.02) * mm});
            skLineSegment(sketch, "E388", {"start": v(-11.54, -7.02) * mm, "end": v(-11.63, -7.15) * mm});
            skLineSegment(sketch, "E389", {"start": v(-11.63, -7.15) * mm, "end": v(-11.72, -7.3) * mm});
            skLineSegment(sketch, "E390", {"start": v(-11.72, -7.3) * mm, "end": v(-11.82, -7.45) * mm});
            skLineSegment(sketch, "E391", {"start": v(-11.82, -7.45) * mm, "end": v(-11.9, -7.61) * mm});
            skLineSegment(sketch, "E392", {"start": v(-11.9, -7.61) * mm, "end": v(-12, -7.79) * mm});
            skLineSegment(sketch, "E393", {"start": v(-12, -7.79) * mm, "end": v(-12.1, -7.98) * mm});
            skLineSegment(sketch, "E394", {"start": v(-12.1, -7.98) * mm, "end": v(-12.2, -8.18) * mm});
            skLineSegment(sketch, "E395", {"start": v(-12.2, -8.18) * mm, "end": v(-12.28, -8.4) * mm});
            skLineSegment(sketch, "E396", {"start": v(-12.28, -8.4) * mm, "end": v(-12.37, -8.62) * mm});
            skLineSegment(sketch, "E397", {"start": v(-12.37, -8.62) * mm, "end": v(-12.46, -8.86) * mm});
            skLineSegment(sketch, "E398", {"start": v(-12.46, -8.86) * mm, "end": v(-12.49, -9.07) * mm});
            skLineSegment(sketch, "E399", {"start": v(-12.49, -9.07) * mm, "end": v(-11.76, -10) * mm});
            skLineSegment(sketch, "E400", {"start": v(-11.76, -10) * mm, "end": v(-11.54, -10.02) * mm});
            skLineSegment(sketch, "E401", {"start": v(-11.54, -10.02) * mm, "end": v(-11.3, -10) * mm});
            skLineSegment(sketch, "E402", {"start": v(-11.3, -10) * mm, "end": v(-11.05, -9.96) * mm});
            skLineSegment(sketch, "E403", {"start": v(-11.05, -9.96) * mm, "end": v(-10.82, -9.92) * mm});
            skLineSegment(sketch, "E404", {"start": v(-10.82, -9.92) * mm, "end": v(-10.6, -9.88) * mm});
            skLineSegment(sketch, "E405", {"start": v(-10.6, -9.88) * mm, "end": v(-10.4, -9.83) * mm});
            skLineSegment(sketch, "E406", {"start": v(-10.4, -9.83) * mm, "end": v(-10.2, -9.78) * mm});
            skLineSegment(sketch, "E407", {"start": v(-10.2, -9.78) * mm, "end": v(-10.02, -9.73) * mm});
            skLineSegment(sketch, "E408", {"start": v(-10.02, -9.73) * mm, "end": v(-9.85, -9.67) * mm});
            skLineSegment(sketch, "E409", {"start": v(-9.85, -9.67) * mm, "end": v(-9.69, -9.62) * mm});
            skLineSegment(sketch, "E410", {"start": v(-9.69, -9.62) * mm, "end": v(-9.54, -9.56) * mm});
            skLineSegment(sketch, "E411", {"start": v(-9.54, -9.56) * mm, "end": v(-9.4, -9.5) * mm});
            skLineSegment(sketch, "E412", {"start": v(-9.4, -9.5) * mm, "end": v(-9.28, -9.44) * mm});
            skLineSegment(sketch, "E413", {"start": v(-9.28, -9.44) * mm, "end": v(-9.17, -9.39) * mm});
            skLineSegment(sketch, "E414", {"start": v(-9.17, -9.39) * mm, "end": v(-9.06, -9.33) * mm});
            skLineSegment(sketch, "E415", {"start": v(-9.06, -9.33) * mm, "end": v(-8.97, -9.28) * mm});
            skLineSegment(sketch, "E416", {"start": v(-8.97, -9.28) * mm, "end": v(-8.89, -9.23) * mm});
            skLineSegment(sketch, "E417", {"start": v(-8.89, -9.23) * mm, "end": v(-8.82, -9.18) * mm});
            skLineSegment(sketch, "E418", {"start": v(-8.82, -9.18) * mm, "end": v(-8.75, -9.14) * mm});
            skLineSegment(sketch, "E419", {"start": v(-8.75, -9.14) * mm, "end": v(-8.7, -9.1) * mm});
            skLineSegment(sketch, "E420", {"start": v(-8.7, -9.1) * mm, "end": v(-8.66, -9.07) * mm});
            skLineSegment(sketch, "E421", {"start": v(-8.66, -9.07) * mm, "end": v(-8.6, -9.02) * mm});
            skLineSegment(sketch, "E422", {"start": v(-8.6, -9.02) * mm, "end": v(-8.59, -9) * mm});
            skLineSegment(sketch, "E423", {"start": v(-8.59, -9) * mm, "end": v(-8.58, -9) * mm});
            skLineSegment(sketch, "E424", {"start": v(-8.58, -9) * mm, "end": v(-7.38, -7.74) * mm});
            skLineSegment(sketch, "E425", {"start": v(-7.38, -7.74) * mm, "end": v(-5.35, -9.26) * mm});
            skLineSegment(sketch, "E426", {"start": v(-5.35, -9.26) * mm, "end": v(-6.22, -10.77) * mm});
            skLineSegment(sketch, "E427", {"start": v(-6.22, -10.77) * mm, "end": v(-6.22, -10.78) * mm});
            skLineSegment(sketch, "E428", {"start": v(-6.22, -10.78) * mm, "end": v(-6.23, -10.8) * mm});
            skLineSegment(sketch, "E429", {"start": v(-6.23, -10.8) * mm, "end": v(-6.25, -10.83) * mm});
            skLineSegment(sketch, "E430", {"start": v(-6.25, -10.83) * mm, "end": v(-6.26, -10.87) * mm});
            skLineSegment(sketch, "E431", {"start": v(-6.26, -10.87) * mm, "end": v(-6.28, -10.92) * mm});
            skLineSegment(sketch, "E432", {"start": v(-6.28, -10.92) * mm, "end": v(-6.3, -10.98) * mm});
            skLineSegment(sketch, "E433", {"start": v(-6.3, -10.98) * mm, "end": v(-6.33, -11.05) * mm});
            skLineSegment(sketch, "E434", {"start": v(-6.33, -11.05) * mm, "end": v(-6.35, -11.13) * mm});
            skLineSegment(sketch, "E435", {"start": v(-6.35, -11.13) * mm, "end": v(-6.38, -11.22) * mm});
            skLineSegment(sketch, "E436", {"start": v(-6.38, -11.22) * mm, "end": v(-6.4, -11.33) * mm});
            skLineSegment(sketch, "E437", {"start": v(-6.4, -11.33) * mm, "end": v(-6.42, -11.44) * mm});
            skLineSegment(sketch, "E438", {"start": v(-6.42, -11.44) * mm, "end": v(-6.45, -11.57) * mm});
            skLineSegment(sketch, "E439", {"start": v(-6.45, -11.57) * mm, "end": v(-6.46, -11.7) * mm});
            skLineSegment(sketch, "E440", {"start": v(-6.46, -11.7) * mm, "end": v(-6.48, -11.85) * mm});
            skLineSegment(sketch, "E441", {"start": v(-6.48, -11.85) * mm, "end": v(-6.5, -12) * mm});
            skLineSegment(sketch, "E442", {"start": v(-6.5, -12) * mm, "end": v(-6.5, -12.18) * mm});
            skLineSegment(sketch, "E443", {"start": v(-6.5, -12.18) * mm, "end": v(-6.5, -12.36) * mm});
            skLineSegment(sketch, "E444", {"start": v(-6.5, -12.36) * mm, "end": v(-6.5, -12.55) * mm});
            skLineSegment(sketch, "E445", {"start": v(-6.5, -12.55) * mm, "end": v(-6.5, -12.75) * mm});
            skLineSegment(sketch, "E446", {"start": v(-6.5, -12.75) * mm, "end": v(-6.49, -12.96) * mm});
            skLineSegment(sketch, "E447", {"start": v(-6.49, -12.96) * mm, "end": v(-6.47, -13.18) * mm});
            skLineSegment(sketch, "E448", {"start": v(-6.47, -13.18) * mm, "end": v(-6.44, -13.41) * mm});
            skLineSegment(sketch, "E449", {"start": v(-6.44, -13.41) * mm, "end": v(-6.4, -13.65) * mm});
            skLineSegment(sketch, "E450", {"start": v(-6.4, -13.65) * mm, "end": v(-6.36, -13.9) * mm});
            skLineSegment(sketch, "E451", {"start": v(-6.36, -13.9) * mm, "end": v(-6.28, -14.1) * mm});
            skLineSegment(sketch, "E452", {"start": v(-6.28, -14.1) * mm, "end": v(-5.18, -14.54) * mm});
            skLineSegment(sketch, "E453", {"start": v(-5.18, -14.54) * mm, "end": v(-4.99, -14.45) * mm});
            skLineSegment(sketch, "E454", {"start": v(-4.99, -14.45) * mm, "end": v(-4.78, -14.3) * mm});
            skLineSegment(sketch, "E455", {"start": v(-4.78, -14.3) * mm, "end": v(-4.6, -14.15) * mm});
            skLineSegment(sketch, "E456", {"start": v(-4.6, -14.15) * mm, "end": v(-4.41, -14) * mm});
            skLineSegment(sketch, "E457", {"start": v(-4.41, -14) * mm, "end": v(-4.24, -13.86) * mm});
            skLineSegment(sketch, "E458", {"start": v(-4.24, -13.86) * mm, "end": v(-4.09, -13.71) * mm});
            skLineSegment(sketch, "E459", {"start": v(-4.09, -13.71) * mm, "end": v(-3.95, -13.57) * mm});
            skLineSegment(sketch, "E460", {"start": v(-3.95, -13.57) * mm, "end": v(-3.81, -13.43) * mm});
            skLineSegment(sketch, "E461", {"start": v(-3.81, -13.43) * mm, "end": v(-3.7, -13.3) * mm});
            skLineSegment(sketch, "E462", {"start": v(-3.7, -13.3) * mm, "end": v(-3.58, -13.17) * mm});
            skLineSegment(sketch, "E463", {"start": v(-3.58, -13.17) * mm, "end": v(-3.48, -13.05) * mm});
            skLineSegment(sketch, "E464", {"start": v(-3.48, -13.05) * mm, "end": v(-3.4, -12.93) * mm});
            skLineSegment(sketch, "E465", {"start": v(-3.4, -12.93) * mm, "end": v(-3.31, -12.82) * mm});
            skLineSegment(sketch, "E466", {"start": v(-3.31, -12.82) * mm, "end": v(-3.24, -12.71) * mm});
            skLineSegment(sketch, "E467", {"start": v(-3.24, -12.71) * mm, "end": v(-3.18, -12.61) * mm});
            skLineSegment(sketch, "E468", {"start": v(-3.18, -12.61) * mm, "end": v(-3.13, -12.52) * mm});
            skLineSegment(sketch, "E469", {"start": v(-3.13, -12.52) * mm, "end": v(-3.08, -12.44) * mm});
            skLineSegment(sketch, "E470", {"start": v(-3.08, -12.44) * mm, "end": v(-3.04, -12.36) * mm});
            skLineSegment(sketch, "E471", {"start": v(-3.04, -12.36) * mm, "end": v(-3, -12.3) * mm});
            skLineSegment(sketch, "E472", {"start": v(-3, -12.3) * mm, "end": v(-2.98, -12.24) * mm});
            skLineSegment(sketch, "E473", {"start": v(-2.98, -12.24) * mm, "end": v(-2.96, -12.19) * mm});
            skLineSegment(sketch, "E474", {"start": v(-2.96, -12.19) * mm, "end": v(-2.95, -12.15) * mm});
            skLineSegment(sketch, "E475", {"start": v(-2.95, -12.15) * mm, "end": v(-2.94, -12.12) * mm});
            skLineSegment(sketch, "E476", {"start": v(-2.94, -12.12) * mm, "end": v(-2.93, -12.1) * mm});
            skLineSegment(sketch, "E477", {"start": v(-2.93, -12.1) * mm, "end": v(-2.93, -12.08) * mm});
            skLineSegment(sketch, "E478", {"start": v(-2.93, -12.08) * mm, "end": v(-2.52, -10.4) * mm});
            skLineSegment(sketch, "E479", {"start": v(-2.52, -10.4) * mm, "end": v(0, -10.7) * mm});
            skLineSegment(sketch, "E480", {"start": v(0, -10.7) * mm, "end": v(0, -12.45) * mm});
            skLineSegment(sketch, "E481", {"start": v(0, -12.45) * mm, "end": v(0, -12.47) * mm});
            skLineSegment(sketch, "E482", {"start": v(0, -12.47) * mm, "end": v(0, -12.5) * mm});
            skLineSegment(sketch, "E483", {"start": v(0, -12.5) * mm, "end": v(0, -12.54) * mm});
            skLineSegment(sketch, "E484", {"start": v(0, -12.54) * mm, "end": v(0.02, -12.6) * mm});
            skLineSegment(sketch, "E485", {"start": v(0.02, -12.6) * mm, "end": v(0.03, -12.66) * mm});
            skLineSegment(sketch, "E486", {"start": v(0.03, -12.66) * mm, "end": v(0.04, -12.73) * mm});
            skLineSegment(sketch, "E487", {"start": v(0.04, -12.73) * mm, "end": v(0.06, -12.81) * mm});
            skLineSegment(sketch, "E488", {"start": v(0.06, -12.81) * mm, "end": v(0.09, -12.9) * mm});
            skLineSegment(sketch, "E489", {"start": v(0.09, -12.9) * mm, "end": v(0.12, -13) * mm});
            skLineSegment(sketch, "E490", {"start": v(0.12, -13) * mm, "end": v(0.16, -13.12) * mm});
            skLineSegment(sketch, "E491", {"start": v(0.16, -13.12) * mm, "end": v(0.2, -13.24) * mm});
            skLineSegment(sketch, "E492", {"start": v(0.2, -13.24) * mm, "end": v(0.25, -13.37) * mm});
            skLineSegment(sketch, "E493", {"start": v(0.25, -13.37) * mm, "end": v(0.31, -13.5) * mm});
            skLineSegment(sketch, "E494", {"start": v(0.31, -13.5) * mm, "end": v(0.38, -13.65) * mm});
            skLineSegment(sketch, "E495", {"start": v(0.38, -13.65) * mm, "end": v(0.46, -13.8) * mm});
            skLineSegment(sketch, "E496", {"start": v(0.46, -13.8) * mm, "end": v(0.54, -13.96) * mm});
            skLineSegment(sketch, "E497", {"start": v(0.54, -13.96) * mm, "end": v(0.64, -14.12) * mm});
            skLineSegment(sketch, "E498", {"start": v(0.64, -14.12) * mm, "end": v(0.74, -14.3) * mm});
            skLineSegment(sketch, "E499", {"start": v(0.74, -14.3) * mm, "end": v(0.86, -14.47) * mm});
            skLineSegment(sketch, "E500", {"start": v(0.86, -14.47) * mm, "end": v(0.99, -14.65) * mm});
            skLineSegment(sketch, "E501", {"start": v(0.99, -14.65) * mm, "end": v(1.13, -14.83) * mm});
            skLineSegment(sketch, "E502", {"start": v(1.13, -14.83) * mm, "end": v(1.28, -15.02) * mm});
            skLineSegment(sketch, "E503", {"start": v(1.28, -15.02) * mm, "end": v(1.44, -15.22) * mm});
            skLineSegment(sketch, "E504", {"start": v(1.44, -15.22) * mm, "end": v(1.61, -15.35) * mm});
            skLineSegment(sketch, "E505", {"start": v(1.61, -15.35) * mm, "end": v(2.78, -15.18) * mm});
            skLineSegment(sketch, "E506", {"start": v(2.78, -15.18) * mm, "end": v(2.9, -15) * mm});
            skLineSegment(sketch, "E507", {"start": v(2.9, -15) * mm, "end": v(3, -14.78) * mm});
            skLineSegment(sketch, "E508", {"start": v(3, -14.78) * mm, "end": v(3.1, -14.55) * mm});
            skLineSegment(sketch, "E509", {"start": v(3.1, -14.55) * mm, "end": v(3.18, -14.33) * mm});
            skLineSegment(sketch, "E510", {"start": v(3.18, -14.33) * mm, "end": v(3.25, -14.12) * mm});
            skLineSegment(sketch, "E511", {"start": v(3.25, -14.12) * mm, "end": v(3.32, -13.92) * mm});
            skLineSegment(sketch, "E512", {"start": v(3.32, -13.92) * mm, "end": v(3.37, -13.73) * mm});
            skLineSegment(sketch, "E513", {"start": v(3.37, -13.73) * mm, "end": v(3.41, -13.54) * mm});
            skLineSegment(sketch, "E514", {"start": v(3.41, -13.54) * mm, "end": v(3.45, -13.37) * mm});
            skLineSegment(sketch, "E515", {"start": v(3.45, -13.37) * mm, "end": v(3.48, -13.2) * mm});
            skLineSegment(sketch, "E516", {"start": v(3.48, -13.2) * mm, "end": v(3.5, -13.04) * mm});
            skLineSegment(sketch, "E517", {"start": v(3.5, -13.04) * mm, "end": v(3.53, -12.9) * mm});
            skLineSegment(sketch, "E518", {"start": v(3.53, -12.9) * mm, "end": v(3.54, -12.76) * mm});
            skLineSegment(sketch, "E519", {"start": v(3.54, -12.76) * mm, "end": v(3.55, -12.63) * mm});
            skLineSegment(sketch, "E520", {"start": v(3.55, -12.63) * mm, "end": v(3.55, -12.51) * mm});
            skLineSegment(sketch, "E521", {"start": v(3.55, -12.51) * mm, "end": v(3.55, -12.4) * mm});
            skLineSegment(sketch, "E522", {"start": v(3.55, -12.4) * mm, "end": v(3.55, -12.31) * mm});
            skLineSegment(sketch, "E523", {"start": v(3.55, -12.31) * mm, "end": v(3.55, -12.23) * mm});
            skLineSegment(sketch, "E524", {"start": v(3.55, -12.23) * mm, "end": v(3.54, -12.15) * mm});
            skLineSegment(sketch, "E525", {"start": v(3.54, -12.15) * mm, "end": v(3.53, -12.09) * mm});
            skLineSegment(sketch, "E526", {"start": v(3.53, -12.09) * mm, "end": v(3.53, -12.04) * mm});
            skLineSegment(sketch, "E527", {"start": v(3.53, -12.04) * mm, "end": v(3.52, -12) * mm});
            skLineSegment(sketch, "E528", {"start": v(3.52, -12) * mm, "end": v(3.51, -11.96) * mm});
            skLineSegment(sketch, "E529", {"start": v(3.51, -11.96) * mm, "end": v(3.5, -11.94) * mm});
            skLineSegment(sketch, "E530", {"start": v(3.5, -11.94) * mm, "end": v(3.5, -11.93) * mm});
            skLineSegment(sketch, "E531", {"start": v(3.5, -11.93) * mm, "end": v(3.02, -10.26) * mm});
            skLineSegment(sketch, "E532", {"start": v(3.02, -10.26) * mm, "end": v(5.35, -9.26) * mm});
            skLineSegment(sketch, "E533", {"start": v(5.35, -9.26) * mm, "end": v(6.22, -10.77) * mm});
            skLineSegment(sketch, "E534", {"start": v(6.22, -10.77) * mm, "end": v(6.22, -10.78) * mm});
            skLineSegment(sketch, "E535", {"start": v(6.22, -10.78) * mm, "end": v(6.24, -10.8) * mm});
            skLineSegment(sketch, "E536", {"start": v(6.24, -10.8) * mm, "end": v(6.25, -10.82) * mm});
            skLineSegment(sketch, "E537", {"start": v(6.25, -10.82) * mm, "end": v(6.28, -10.86) * mm});
            skLineSegment(sketch, "E538", {"start": v(6.28, -10.86) * mm, "end": v(6.31, -10.9) * mm});
            skLineSegment(sketch, "E539", {"start": v(6.31, -10.9) * mm, "end": v(6.35, -10.95) * mm});
            skLineSegment(sketch, "E540", {"start": v(6.35, -10.95) * mm, "end": v(6.4, -11) * mm});
            skLineSegment(sketch, "E541", {"start": v(6.4, -11) * mm, "end": v(6.46, -11.07) * mm});
            skLineSegment(sketch, "E542", {"start": v(6.46, -11.07) * mm, "end": v(6.53, -11.13) * mm});
            skLineSegment(sketch, "E543", {"start": v(6.53, -11.13) * mm, "end": v(6.6, -11.2) * mm});
            skLineSegment(sketch, "E544", {"start": v(6.6, -11.2) * mm, "end": v(6.7, -11.28) * mm});
            skLineSegment(sketch, "E545", {"start": v(6.7, -11.28) * mm, "end": v(6.8, -11.36) * mm});
            skLineSegment(sketch, "E546", {"start": v(6.8, -11.36) * mm, "end": v(6.9, -11.45) * mm});
            skLineSegment(sketch, "E547", {"start": v(6.9, -11.45) * mm, "end": v(7.02, -11.54) * mm});
            skLineSegment(sketch, "E548", {"start": v(7.02, -11.54) * mm, "end": v(7.15, -11.63) * mm});
            skLineSegment(sketch, "E549", {"start": v(7.15, -11.63) * mm, "end": v(7.3, -11.72) * mm});
            skLineSegment(sketch, "E550", {"start": v(7.3, -11.72) * mm, "end": v(7.45, -11.82) * mm});
            skLineSegment(sketch, "E551", {"start": v(7.45, -11.82) * mm, "end": v(7.61, -11.9) * mm});
            skLineSegment(sketch, "E552", {"start": v(7.61, -11.9) * mm, "end": v(7.79, -12) * mm});
            skLineSegment(sketch, "E553", {"start": v(7.79, -12) * mm, "end": v(7.98, -12.1) * mm});
            skLineSegment(sketch, "E554", {"start": v(7.98, -12.1) * mm, "end": v(8.18, -12.2) * mm});
            skLineSegment(sketch, "E555", {"start": v(8.18, -12.2) * mm, "end": v(8.4, -12.28) * mm});
            skLineSegment(sketch, "E556", {"start": v(8.4, -12.28) * mm, "end": v(8.62, -12.37) * mm});
            skLineSegment(sketch, "E557", {"start": v(8.62, -12.37) * mm, "end": v(8.86, -12.46) * mm});
            skLineSegment(sketch, "E558", {"start": v(8.86, -12.46) * mm, "end": v(9.07, -12.49) * mm});
            skLineSegment(sketch, "E559", {"start": v(9.07, -12.49) * mm, "end": v(10, -11.76) * mm});
            skLineSegment(sketch, "E560", {"start": v(10, -11.76) * mm, "end": v(10.02, -11.54) * mm});
            skLineSegment(sketch, "E561", {"start": v(10.02, -11.54) * mm, "end": v(10, -11.3) * mm});
            skLineSegment(sketch, "E562", {"start": v(10, -11.3) * mm, "end": v(9.96, -11.05) * mm});
            skLineSegment(sketch, "E563", {"start": v(9.96, -11.05) * mm, "end": v(9.92, -10.82) * mm});
            skLineSegment(sketch, "E564", {"start": v(9.92, -10.82) * mm, "end": v(9.88, -10.6) * mm});
            skLineSegment(sketch, "E565", {"start": v(9.88, -10.6) * mm, "end": v(9.83, -10.4) * mm});
            skLineSegment(sketch, "E566", {"start": v(9.83, -10.4) * mm, "end": v(9.78, -10.2) * mm});
            skLineSegment(sketch, "E567", {"start": v(9.78, -10.2) * mm, "end": v(9.73, -10.02) * mm});
            skLineSegment(sketch, "E568", {"start": v(9.73, -10.02) * mm, "end": v(9.67, -9.85) * mm});
            skLineSegment(sketch, "E569", {"start": v(9.67, -9.85) * mm, "end": v(9.62, -9.69) * mm});
            skLineSegment(sketch, "E570", {"start": v(9.62, -9.69) * mm, "end": v(9.56, -9.54) * mm});
            skLineSegment(sketch, "E571", {"start": v(9.56, -9.54) * mm, "end": v(9.5, -9.4) * mm});
            skLineSegment(sketch, "E572", {"start": v(9.5, -9.4) * mm, "end": v(9.44, -9.28) * mm});
            skLineSegment(sketch, "E573", {"start": v(9.44, -9.28) * mm, "end": v(9.39, -9.17) * mm});
            skLineSegment(sketch, "E574", {"start": v(9.39, -9.17) * mm, "end": v(9.33, -9.06) * mm});
            skLineSegment(sketch, "E575", {"start": v(9.33, -9.06) * mm, "end": v(9.28, -8.97) * mm});
            skLineSegment(sketch, "E576", {"start": v(9.28, -8.97) * mm, "end": v(9.23, -8.89) * mm});
            skLineSegment(sketch, "E577", {"start": v(9.23, -8.89) * mm, "end": v(9.18, -8.82) * mm});
            skLineSegment(sketch, "E578", {"start": v(9.18, -8.82) * mm, "end": v(9.14, -8.75) * mm});
            skLineSegment(sketch, "E579", {"start": v(9.14, -8.75) * mm, "end": v(9.1, -8.7) * mm});
            skLineSegment(sketch, "E580", {"start": v(9.1, -8.7) * mm, "end": v(9.07, -8.66) * mm});
            skLineSegment(sketch, "E581", {"start": v(9.07, -8.66) * mm, "end": v(9.02, -8.6) * mm});
            skLineSegment(sketch, "E582", {"start": v(9.02, -8.6) * mm, "end": v(9, -8.59) * mm});
            skLineSegment(sketch, "E583", {"start": v(9, -8.59) * mm, "end": v(9, -8.58) * mm});
            skLineSegment(sketch, "E584", {"start": v(9, -8.58) * mm, "end": v(7.74, -7.38) * mm});
            skLineSegment(sketch, "E585", {"start": v(7.74, -7.38) * mm, "end": v(9.26, -5.35) * mm});
            skLineSegment(sketch, "E586", {"start": v(9.26, -5.35) * mm, "end": v(10.77, -6.22) * mm});
            skLineSegment(sketch, "E587", {"start": v(10.77, -6.22) * mm, "end": v(10.78, -6.22) * mm});
            skLineSegment(sketch, "E588", {"start": v(10.78, -6.22) * mm, "end": v(10.8, -6.23) * mm});
            skLineSegment(sketch, "E589", {"start": v(10.8, -6.23) * mm, "end": v(10.83, -6.25) * mm});
            skLineSegment(sketch, "E590", {"start": v(10.83, -6.25) * mm, "end": v(10.87, -6.26) * mm});
            skLineSegment(sketch, "E591", {"start": v(10.87, -6.26) * mm, "end": v(10.92, -6.28) * mm});
            skLineSegment(sketch, "E592", {"start": v(10.92, -6.28) * mm, "end": v(10.98, -6.3) * mm});
            skLineSegment(sketch, "E593", {"start": v(10.98, -6.3) * mm, "end": v(11.05, -6.33) * mm});
            skLineSegment(sketch, "E594", {"start": v(11.05, -6.33) * mm, "end": v(11.13, -6.35) * mm});
            skLineSegment(sketch, "E595", {"start": v(11.13, -6.35) * mm, "end": v(11.22, -6.38) * mm});
            skLineSegment(sketch, "E596", {"start": v(11.22, -6.38) * mm, "end": v(11.33, -6.4) * mm});
            skLineSegment(sketch, "E597", {"start": v(11.33, -6.4) * mm, "end": v(11.44, -6.42) * mm});
            skLineSegment(sketch, "E598", {"start": v(11.44, -6.42) * mm, "end": v(11.57, -6.45) * mm});
            skLineSegment(sketch, "E599", {"start": v(11.57, -6.45) * mm, "end": v(11.7, -6.46) * mm});
            skLineSegment(sketch, "E600", {"start": v(11.7, -6.46) * mm, "end": v(11.85, -6.48) * mm});
            skLineSegment(sketch, "E601", {"start": v(11.85, -6.48) * mm, "end": v(12, -6.5) * mm});
            skLineSegment(sketch, "E602", {"start": v(12, -6.5) * mm, "end": v(12.18, -6.5) * mm});
            skLineSegment(sketch, "E603", {"start": v(12.18, -6.5) * mm, "end": v(12.36, -6.5) * mm});
            skLineSegment(sketch, "E604", {"start": v(12.36, -6.5) * mm, "end": v(12.55, -6.5) * mm});
            skLineSegment(sketch, "E605", {"start": v(12.55, -6.5) * mm, "end": v(12.75, -6.5) * mm});
            skLineSegment(sketch, "E606", {"start": v(12.75, -6.5) * mm, "end": v(12.96, -6.49) * mm});
            skLineSegment(sketch, "E607", {"start": v(12.96, -6.49) * mm, "end": v(13.18, -6.47) * mm});
            skLineSegment(sketch, "E608", {"start": v(13.18, -6.47) * mm, "end": v(13.41, -6.44) * mm});
            skLineSegment(sketch, "E609", {"start": v(13.41, -6.44) * mm, "end": v(13.65, -6.4) * mm});
            skLineSegment(sketch, "E610", {"start": v(13.65, -6.4) * mm, "end": v(13.9, -6.36) * mm});
            skLineSegment(sketch, "E611", {"start": v(13.9, -6.36) * mm, "end": v(14.1, -6.28) * mm});
            skLineSegment(sketch, "E612", {"start": v(14.1, -6.28) * mm, "end": v(14.54, -5.18) * mm});
            skLineSegment(sketch, "E613", {"start": v(14.54, -5.18) * mm, "end": v(14.45, -4.99) * mm});
            skLineSegment(sketch, "E614", {"start": v(14.45, -4.99) * mm, "end": v(14.3, -4.78) * mm});
            skLineSegment(sketch, "E615", {"start": v(14.3, -4.78) * mm, "end": v(14.15, -4.6) * mm});
            skLineSegment(sketch, "E616", {"start": v(14.15, -4.6) * mm, "end": v(14, -4.41) * mm});
            skLineSegment(sketch, "E617", {"start": v(14, -4.41) * mm, "end": v(13.86, -4.24) * mm});
            skLineSegment(sketch, "E618", {"start": v(13.86, -4.24) * mm, "end": v(13.71, -4.09) * mm});
            skLineSegment(sketch, "E619", {"start": v(13.71, -4.09) * mm, "end": v(13.57, -3.95) * mm});
            skLineSegment(sketch, "E620", {"start": v(13.57, -3.95) * mm, "end": v(13.43, -3.81) * mm});
            skLineSegment(sketch, "E621", {"start": v(13.43, -3.81) * mm, "end": v(13.3, -3.7) * mm});
            skLineSegment(sketch, "E622", {"start": v(13.3, -3.7) * mm, "end": v(13.17, -3.58) * mm});
            skLineSegment(sketch, "E623", {"start": v(13.17, -3.58) * mm, "end": v(13.05, -3.48) * mm});
            skLineSegment(sketch, "E624", {"start": v(13.05, -3.48) * mm, "end": v(12.93, -3.4) * mm});
            skLineSegment(sketch, "E625", {"start": v(12.93, -3.4) * mm, "end": v(12.82, -3.31) * mm});
            skLineSegment(sketch, "E626", {"start": v(12.82, -3.31) * mm, "end": v(12.71, -3.24) * mm});
            skLineSegment(sketch, "E627", {"start": v(12.71, -3.24) * mm, "end": v(12.61, -3.18) * mm});
            skLineSegment(sketch, "E628", {"start": v(12.61, -3.18) * mm, "end": v(12.52, -3.13) * mm});
            skLineSegment(sketch, "E629", {"start": v(12.52, -3.13) * mm, "end": v(12.44, -3.08) * mm});
            skLineSegment(sketch, "E630", {"start": v(12.44, -3.08) * mm, "end": v(12.36, -3.04) * mm});
            skLineSegment(sketch, "E631", {"start": v(12.36, -3.04) * mm, "end": v(12.3, -3) * mm});
            skLineSegment(sketch, "E632", {"start": v(12.3, -3) * mm, "end": v(12.24, -2.98) * mm});
            skLineSegment(sketch, "E633", {"start": v(12.24, -2.98) * mm, "end": v(12.19, -2.96) * mm});
            skLineSegment(sketch, "E634", {"start": v(12.19, -2.96) * mm, "end": v(12.15, -2.95) * mm});
            skLineSegment(sketch, "E635", {"start": v(12.15, -2.95) * mm, "end": v(12.12, -2.94) * mm});
            skLineSegment(sketch, "E636", {"start": v(12.12, -2.94) * mm, "end": v(12.1, -2.93) * mm});
            skLineSegment(sketch, "E637", {"start": v(12.1, -2.93) * mm, "end": v(12.08, -2.93) * mm});
            skLineSegment(sketch, "E638", {"start": v(12.08, -2.93) * mm, "end": v(10.4, -2.52) * mm});
            skLineSegment(sketch, "E639", {"start": v(10.4, -2.52) * mm, "end": v(10.7, 0) * mm});
            skCircle(sketch, "E640", {"center": v(0, 0) * mm, "radius": 1.97 * mm});
            skSolve(sketch);
        }
        {
            var Q0;
            Q0=makeQuery(id+"F0.imprint","IMPRINT",FACE,{"disambiguationData":[TD([[makeQuery(id+"F0.imprint","IMPRINT",EDGE,{"derivedFrom":sQuery(id+"F0.wireOp",EDGE,"E0")}),1.0]])]});
            extrude(context, id + "F1", {"entities" : qUnion([Q0]), "depth" : 6.5 * mm, "offsetDistance" : 25 * mm});
        }
    });
